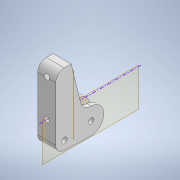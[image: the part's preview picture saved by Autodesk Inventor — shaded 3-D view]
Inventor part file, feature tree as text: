
AUTODESK INVENTOR PART (.ipt)
format: ipt  version: 2022.2 (Build 262287000, 287)  size: 334,336 bytes
history: native  units: mm
features: sketch x7, extrude x5, other x4, projected_geometry x3, plane x2, hole x1, fillet x1, reference x1
ambient origin geometry x8: Origin, YZ Plane, XZ Plane, XY Plane, X Axis, Y Axis, Z Axis, Center Point
bodies: Solid1 (feature_tree)
feature tree (24):
  other  "Motor.ipt"
  extrude  "Extrusion1"  Depth=3.3mm
  extrude  "Extrusion2"  Depth=10.0mm
  extrude  "Extrusion3"  Depth=5.0mm
  plane  "Work Plane1"
  sketch  "Sketch5"  dims[d7=15.0mm d8=3.3mm d13=2.5mm d14=0.0mm]
  hole  "Hole1"  [1 undecoded]
  fillet  "Fillet1"  Radius=2.5mm
  extrude  "Extrusion5"  Depth=5.5mm TaperAngle=0.0deg
  plane  "Work Plane2"
  extrude  "Extrusion6"  Depth=4.0mm
  sketch  "Sketch1"  dims[d0=16.0mm d1=3.3mm]
  sketch  "Sketch2"  dims[d2=10.0mm d3=15.500005mm]
  projected_geometry  "Projected Loop1"
  sketch  "Sketch3"  dims[d4=2.000005mm d6=5.0mm]
  projected_geometry  "Projected Loop2"
  projected_geometry  "Projected Loop3"
  sketch  "Sketch6"  dims[d15=5.5mm d16=0.0mm d20=2.5mm d21=0.0mm]
  sketch  "Sketch7"  dims[d28=3.0mm d29=6.0mm d30=4.0mm d31=2.0mm d32=90.0deg d33=8.0mm d34=20.594885mm d35=4.0mm]
  reference  "Reference1"
  sketch  "Sketch9"  dims[d36=2.0mm d37=3.0mm d39=32.0mm d40=0.0mm d41=0.0mm d42=-10.0mm d43=5.5mm d44=4.0mm d45=0.0mm]
  other  "<userpath>\Documents\Inventor\Wire Bender\Assembly.iam"
  other  "Assembly.iam"
  other  "Feed Motor Mount:1"
note: 1 required parameter value undecoded (feature->parameter linkage not recoverable at this tier; creation-order binding heuristic only, values carry confidence <= 0.55)
